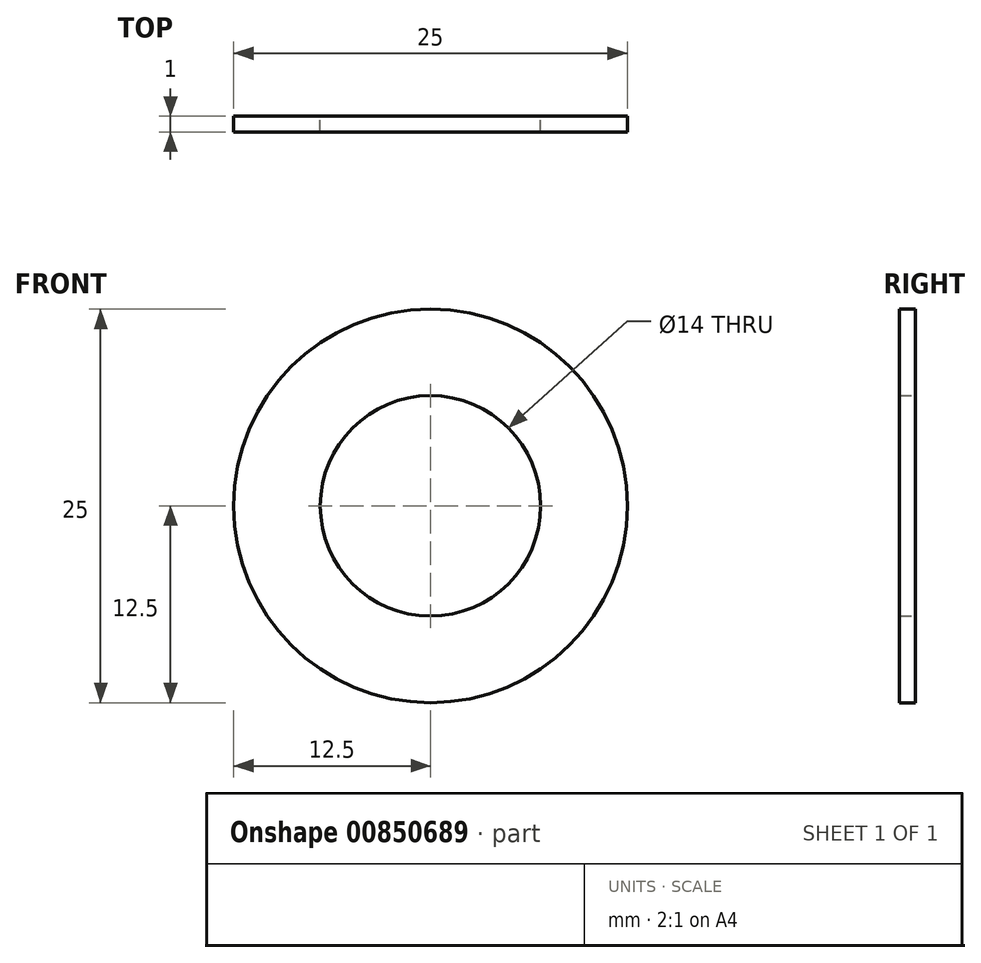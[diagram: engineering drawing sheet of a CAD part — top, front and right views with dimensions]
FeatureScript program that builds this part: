
annotation { "Feature Type Name" : "Feature", "Feature Type Description" : "" }
export const myFeature = defineFeature(function(context is Context, id is Id, definition is map)
    precondition{}
    {
        {
            var Q0;
            Q0=qCreatedBy(makeId("Front.planeOp"),FACE);
            var sketch = newSketch(context, id + "F0", { "sketchPlane" : qUnion([Q0])});
            skCircle(sketch, "E0", {"center": v(0, 0) * mm, "radius": 12.5 * mm});
            skCircle(sketch, "E1", {"center": v(0, 0) * mm, "radius": 7 * mm});
            skSolve(sketch);
        }
        {
            var Q0;
            Q0 = qSketchRegion(id + "F0", true);
            extrude(context, id + "F1", {"entities" : qUnion([Q0]), "depth" : 1 * mm, "offsetDistance" : 25 * mm});
        }
    });
